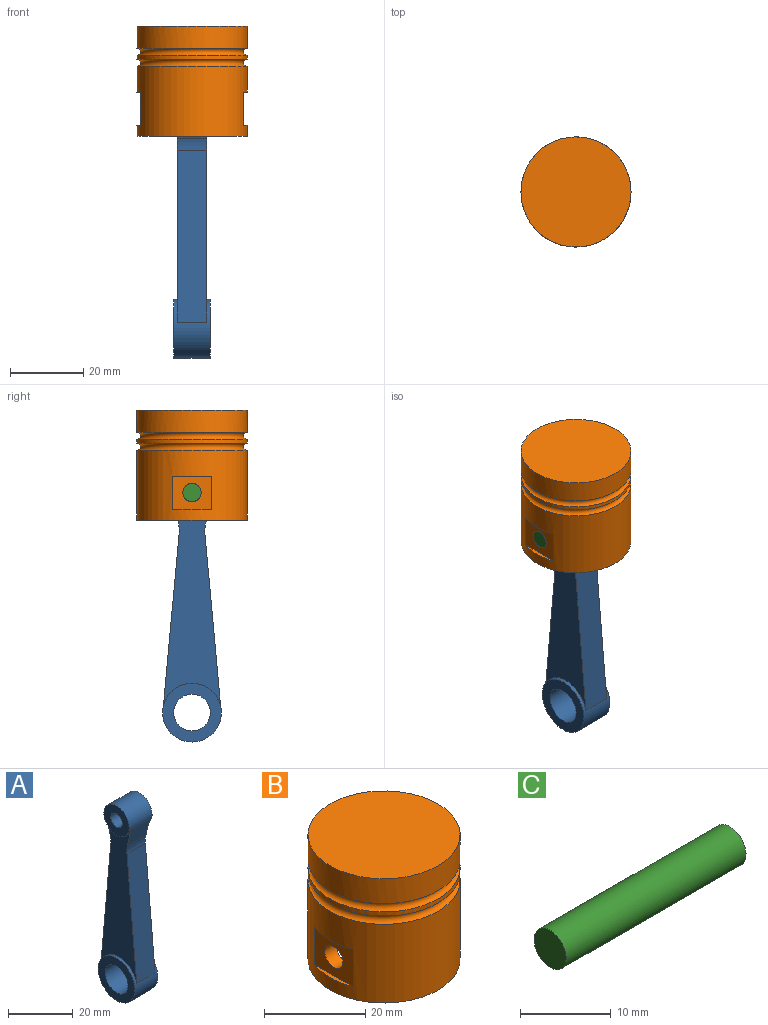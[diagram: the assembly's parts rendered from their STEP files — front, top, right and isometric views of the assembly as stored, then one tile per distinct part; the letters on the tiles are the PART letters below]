
ASSEMBLY  parts=3 mates=2
PART A: 16 faces, bbox 10x16x73.5 mm
  f0: cylinder r=8mm len=16mm, axis (-1,0,0), area 330.6mm2, adj f2,f3,f9,f10,f12,f13
  f1: cylinder r=5mm len=10mm, axis (-1,0,0), area 314.2mm2, adj f2,f3
  f2: plane 16x16mm, normal (1,0,0), area 122.5mm2, adj f0,f1
  f3: plane 16x16mm, normal (-1,0,0), area 122.5mm2, adj f0,f1
  f4: cylinder r=5.5mm len=11mm, axis (-1,0,0), area 227.3mm2, adj f6,f7,f8,f11,f12,f13
  f5: cylinder r=2.5mm len=10mm, axis (-1,0,0), area 157.1mm2, adj f6,f7
  f6: plane 11x11mm, normal (1,0,0), area 75.4mm2, adj f4,f5
  f7: plane 11x11mm, normal (-1,0,0), area 75.4mm2, adj f4,f5
  f8: plane 8x6.95mm, normal (0,-0.97,-0.23), area 57mm2, adj f4,f12,f13,f14
  f9: plane 46.86x8mm, normal (0,-1,0.09), area 376.4mm2, adj f0,f12,f13,f14
  f10: plane 46.84x8mm, normal (0,1,0.09), area 376.2mm2, adj f0,f12,f13,f15
  f11: plane 8x6.97mm, normal (0,0.97,-0.23), area 57.2mm2, adj f4,f12,f13,f15
  f12: plane 56.96x15.59mm, normal (1,0,0), area 510.7mm2, adj f0,f4,f8,f9,f10,f11,f14,f15
  f13: plane 56.96x15.59mm, normal (-1,0,0), area 510.7mm2, adj f0,f4,f8,f9,f10,f11,f14,f15
  f14: cylinder r=10mm len=8mm, axis (-1,0,0), area 25.4mm2, adj f8,f9,f12,f13
  f15: cylinder r=10mm len=8mm, axis (1,0,0), area 25.4mm2, adj f10,f11,f12,f13
PART B: 17 faces, bbox 34x34x30 mm
  f0: cylinder r=15mm len=30mm, axis (0,0,-1), area 1592.4mm2, adj f2,f4,f5,f6,f7,f8,f9,f10
  f1: cylinder r=11mm len=22mm, axis (0,0,1), area 997.3mm2, adj f2,f3,f15,f16
  f2: plane 30x30mm, normal (0,0,-1), area 326.7mm2, adj f0,f1
  f3: plane 22x22mm, normal (0,0,-1), area 380.1mm2, adj f1
  f4: plane 10.77x1mm, normal (0,0,-1), area 7.2mm2, adj f0,f6
  f5: plane 10.77x1mm, normal (0,0,1), area 7.2mm2, adj f0,f6
  f6: plane 10.77x9mm, normal (-1,0,0), area 77.3mm2, adj f0,f4,f5,f16
  f7: plane 10.77x1mm, normal (0,0,-1), area 7.2mm2, adj f0,f8
  f8: plane 10.77x9mm, normal (1,0,0), area 77.3mm2, adj f0,f7,f9,f15
  f9: plane 10.77x1mm, normal (0,0,1), area 7.2mm2, adj f0,f8
  f10: torus R=15mm, axis (0,0,1), area 283.5mm2, adj f0,f11
  f11: cylinder r=15mm len=30mm, axis (0,0,-1), area 94.2mm2, adj f10,f12
  f12: torus R=15mm, axis (0,0,1), area 283.5mm2, adj f11,f14
  f13: plane 30x30mm, normal (0,0,1), area 706.9mm2, adj f14
  f14: cylinder r=15mm len=30mm, axis (0,0,-1), area 565.5mm2, adj f12,f13
  f15: cylinder r=2.5mm len=5mm, axis (-1,0,0), area 49.4mm2, adj f1,f8
  f16: cylinder r=2.5mm len=5mm, axis (-1,0,0), area 49.4mm2, adj f1,f6
PART C: 3 faces, bbox 28x5x5 mm
  f0: cylinder r=2.5mm len=28mm, axis (-1,0,0), area 439.8mm2, adj f1,f2
  f1: plane 5x5mm, normal (1,0,0), area 19.6mm2, adj f0
  f2: plane 5x5mm, normal (-1,0,0), area 19.6mm2, adj f0
PLACE A t=(-2.15,14.74,-9.78)mm
PLACE B t=(-2.15,14.74,57.72)mm
PLACE C t=(-2.15,14.74,50.22)mm
MATE revolute B.f15 <-> C.f0  axis (1,0,0) through (11.85,14.74,50.22)mm
MATE revolute C.f0 <-> A.f5  axis (-1,0,0) through (-2.15,14.74,50.22)mm
